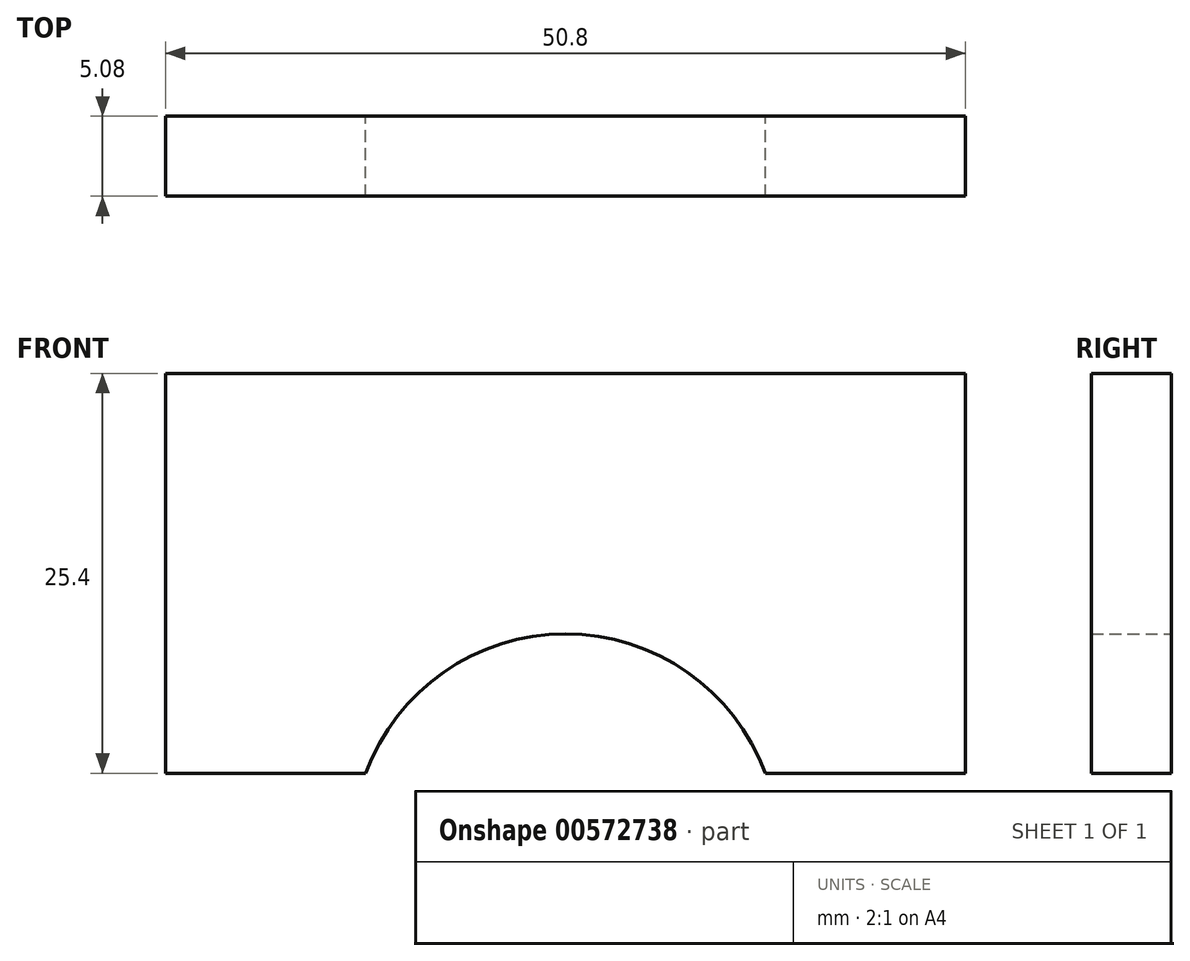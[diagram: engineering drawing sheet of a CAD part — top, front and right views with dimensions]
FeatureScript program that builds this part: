
annotation { "Feature Type Name" : "Feature", "Feature Type Description" : "" }
export const myFeature = defineFeature(function(context is Context, id is Id, definition is map)
    precondition{}
    {
        {
            var Q0;
            Q0=qCreatedBy(makeId("Front.planeOp"),FACE);
            var sketch = newSketch(context, id + "F0", { "sketchPlane" : qUnion([Q0])});
            skLineSegment(sketch, "E0.bottom", {"start": v(-25.4, 12.7) * mm, "end": v(25.4, 12.7) * mm});
            skLineSegment(sketch, "E0.left", {"start": v(-25.4, 12.7) * mm, "end": v(-25.4, -12.7) * mm});
            skLineSegment(sketch, "E0.right", {"start": v(25.4, 12.7) * mm, "end": v(25.4, -12.7) * mm});
            skPoint(sketch, "E0.middle", {"position": v(0, 0) * mm});
            skLineSegment(sketch, "E1", {"start": v(-25.4, -12.7) * mm, "end": v(-12.7, -12.7) * mm});
            skLineSegment(sketch, "E2", {"start": v(25.4, -12.7) * mm, "end": v(12.7, -12.7) * mm});
            skArc(sketch, "E3", {"start": v(12.7, -12.7) * mm, "mid": v(0, -3.85) * mm, "end": v(-12.7, -12.7) * mm});
            skSolve(sketch);
        }
        {
            var Q0;
            Q0=makeQuery(id+"F0.imprint","IMPRINT",FACE,{"disambiguationData":[TD([[makeQuery(id+"F0.imprint","IMPRINT",EDGE,{"derivedFrom":sQuery(id+"F0.wireOp",EDGE,"E0.bottom")}),-1.0]])]});
            extrude(context, id + "F1", {"entities" : qUnion([Q0]), "depth" : 5.08 * mm, "offsetDistance" : 25.4 * mm});
        }
    });
